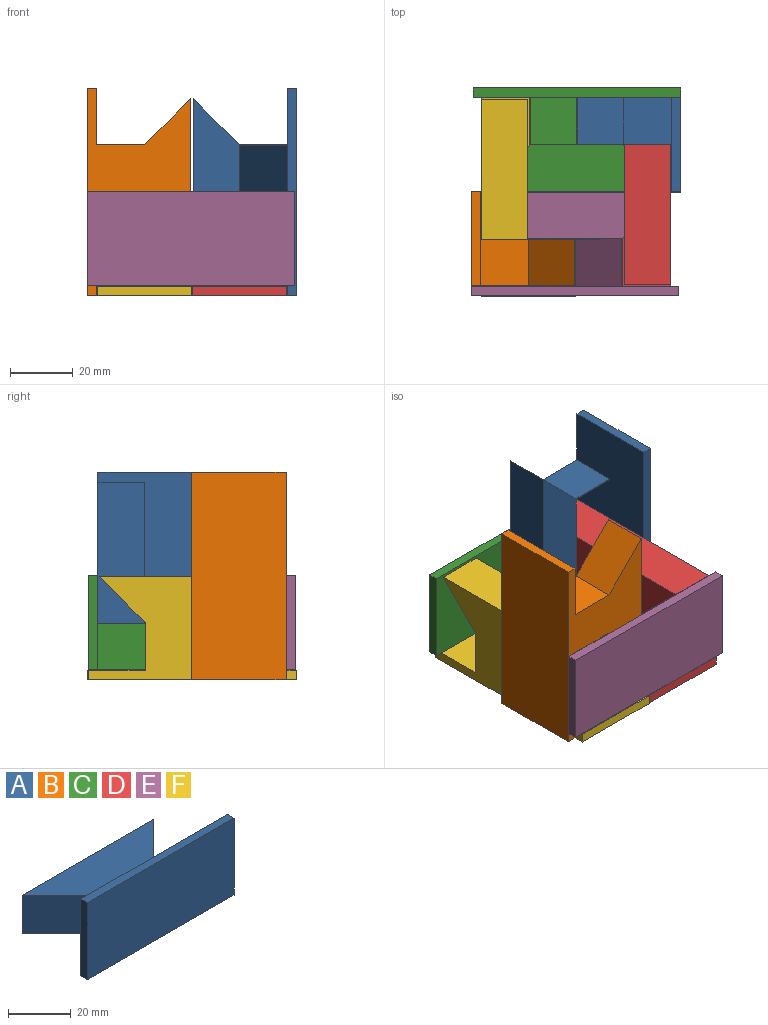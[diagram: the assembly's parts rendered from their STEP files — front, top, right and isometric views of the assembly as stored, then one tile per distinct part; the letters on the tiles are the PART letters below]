
ASSEMBLY  parts=6 mates=4
PART A: 16 faces, bbox 66x32.9x30 mm
  f0: plane 15.28x14.8mm, normal (1,0,0), area 226.2mm2, adj f2,f4,f6,f11
  f1: plane 15.28x14.8mm, normal (-1,0,0), area 226.2mm2, adj f2,f3,f6,f11
  f2: plane 59.23x29.9mm, normal (0,0,1), area 663.7mm2, adj f0,f1,f3,f4,f5,f7,f9,f10
  f3: plane 14.8x14.62mm, normal (-0.71,-0.71,0), area 305.9mm2, adj f1,f2,f5,f6
  f4: plane 14.8x14.62mm, normal (0.71,-0.71,0), area 305.9mm2, adj f0,f2,f5,f6
  f5: plane 59.23x14.8mm, normal (0,1,0), area 876.7mm2, adj f2,f3,f4,f6
  f6: plane 66x32.9mm, normal (0,0,-1), area 1308.7mm2, adj f0,f1,f3,f4,f5,f11,f12,f14
  f7: plane 15.1x14.6mm, normal (0.71,0,0.71), area 311.8mm2, adj f2,f8,f10,f11
  f8: plane 15.1x0.4mm, normal (0,0,1), area 6mm2, adj f7,f9,f10,f11
  f9: plane 15.1x14.6mm, normal (-0.71,0,0.71), area 311.8mm2, adj f2,f8,f10,f11
  f10: plane 29.6x14.6mm, normal (0,-1,0), area 219mm2, adj f2,f7,f8,f9
  f11: plane 66x30mm, normal (0,1,0), area 1755mm2, adj f0,f1,f2,f6,f7,f8,f9,f13
  f12: plane 66x30mm, normal (0,-1,0), area 1980mm2, adj f6,f13,f14,f15
  f13: plane 66x3mm, normal (0,0,1), area 198mm2, adj f11,f12,f14,f15
  f14: plane 30x3mm, normal (-1,0,0), area 90mm2, adj f6,f11,f12,f13
  f15: plane 30x3mm, normal (1,0,0), area 90mm2, adj f6,f11,f12,f13
PART B: same geometry as A
PART C: same geometry as A
PART D: same geometry as A
PART E: same geometry as A
PART F: same geometry as A
PLACE A rot(axis=(0.58,-0.58,0.58),120deg) t=(-16.25,45.96,-27.25)mm
PLACE B rot(axis=(-0.58,-0.58,-0.58),120deg) t=(-46.96,-13.86,-27.21)mm
PLACE C rot(axis=(0,0,1),180deg) t=(-16.34,31.11,-42.05)mm
PLACE D rot(axis=(0.58,-0.58,-0.58),120deg) t=(-1.4,31.15,-27.34)mm
PLACE E rot(axis=(-0.88,0.47,0),0deg) t=(-46.86,0.99,-42.02)mm
PLACE F rot(axis=(0.58,0.58,0.58),120deg) t=(-61.81,0.95,-27.3)mm
MATE fastened D.f3 <-> A.f7  axis (0,0.71,-0.71) through (-8.8,38.46,-19.75)mm
MATE fastened C.f7 <-> A.f3  axis (-0.71,0,0.71) through (-23.84,38.56,-34.55)mm
MATE fastened E.f7 <-> B.f3  axis (0.71,0,0.71) through (-39.36,-6.46,-34.52)mm
MATE fastened F.f3 <-> B.f7  axis (0,-0.71,-0.71) through (-54.41,-6.36,-19.71)mm
